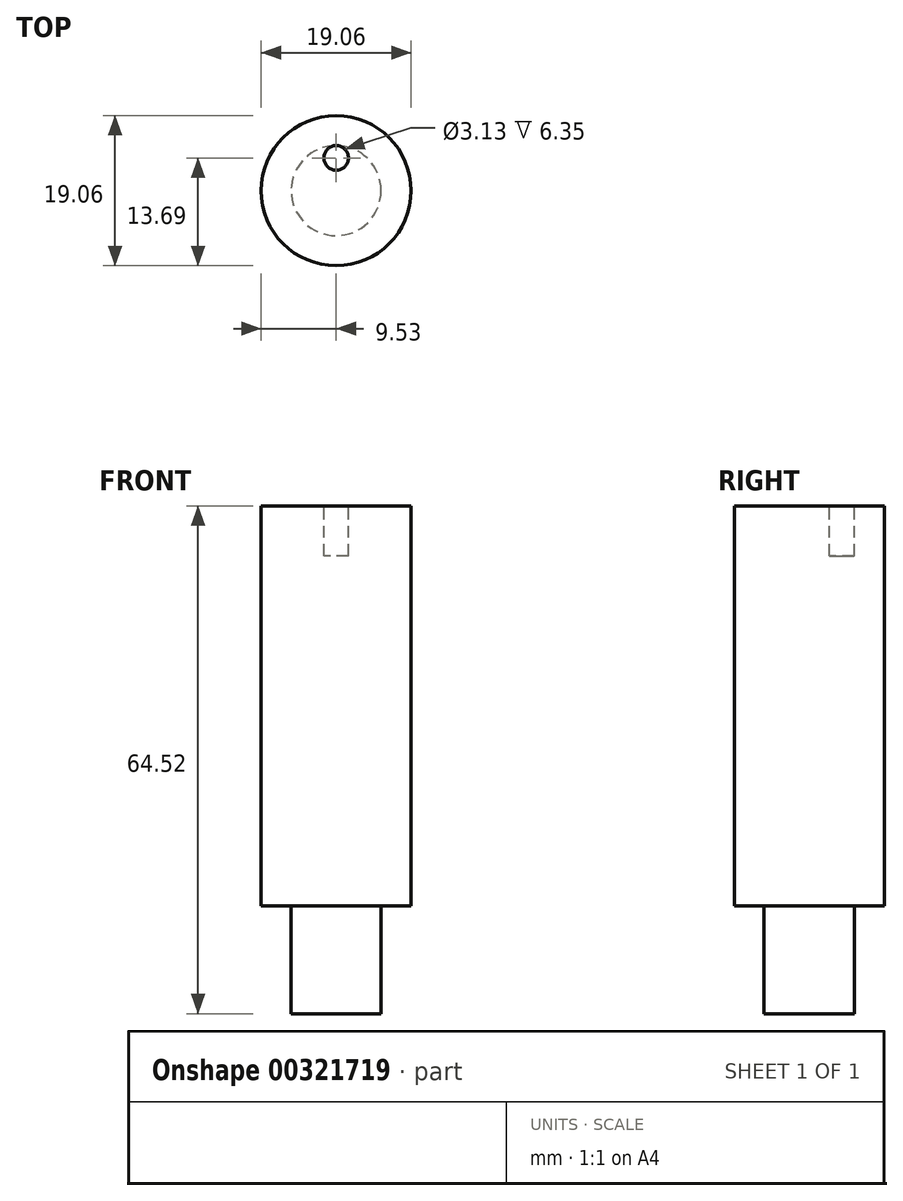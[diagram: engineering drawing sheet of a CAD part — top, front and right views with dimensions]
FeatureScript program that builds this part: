
annotation { "Feature Type Name" : "Feature", "Feature Type Description" : "" }
export const myFeature = defineFeature(function(context is Context, id is Id, definition is map)
    precondition{}
    {
        {
            var Q0;
            Q0=qCreatedBy(makeId("Top.planeOp"),FACE);
            var sketch = newSketch(context, id + "F0", { "sketchPlane" : qUnion([Q0])});
            skCircle(sketch, "E0", {"center": v(0, 0) * mm, "radius": 5.71 * mm});
            skSolve(sketch);
        }
        {
            var Q0;
            Q0=makeQuery(id+"F0.imprint","IMPRINT",FACE,{"disambiguationData":[TD([[makeQuery(id+"F0.imprint","IMPRINT",EDGE,{"derivedFrom":sQuery(id+"F0.wireOp",EDGE,"E0")}),1.0]])]});
            extrude(context, id + "F1", {"entities" : qUnion([Q0]), "depth" : 13.72 * mm});
        }
        {
            var Q0;
            Q0=makeQuery(id+"F1.opExtrude","CAP_FACE",FACE,{"disambiguationData":[OSD([sQuery(id+"F0.wireOp",EDGE,"E0")])],"isStart":false});
            var sketch = newSketch(context, id + "F2", { "sketchPlane" : qUnion([Q0])});
            skCircle(sketch, "E1", {"center": v(0, 0) * mm, "radius": 9.53 * mm});
            skSolve(sketch);
        }
        {
            var Q0;
            Q0=makeQuery(id+"F2.imprint","IMPRINT",FACE,{"disambiguationData":[TD([[makeQuery(id+"F2.imprint","IMPRINT",EDGE,{"derivedFrom":sQuery(id+"F2.wireOp",EDGE,"E1")}),1.0]])]});
            var Q1;
            Q1=makeQuery(id+"F2.imprint","IMPRINT",FACE,{"disambiguationData":[TD([[makeQuery(id+"F2.imprint","IMPRINT",EDGE,{"derivedFrom":makeQuery(id+"F1.opExtrude","CAP_EDGE",EDGE,{"disambiguationData":[OSD([sQuery(id+"F0.wireOp",EDGE,"E0")])],"isStart":false})}),1.0]])]});
            extrude(context, id + "F3", {"entities" : qUnion([Q0, Q1]), "operationType" : NewBodyOperationType.ADD, "depth" : 50.8 * mm});
        }
        {
            var Q0;
            Q0=makeQuery(id+"F3.opExtrude","CAP_FACE",FACE,{"disambiguationData":[OSD([sQuery(id+"F2.wireOp",EDGE,"E1")])],"isStart":false});
            var sketch = newSketch(context, id + "F4", { "sketchPlane" : qUnion([Q0])});
            skCircle(sketch, "E2", {"center": v(0, 4.16) * mm, "radius": 1.56 * mm});
            skSolve(sketch);
        }
        {
            var Q0;
            Q0=makeQuery(id+"F4.imprint","IMPRINT",FACE,{"disambiguationData":[TD([[makeQuery(id+"F4.imprint","IMPRINT",EDGE,{"derivedFrom":sQuery(id+"F4.wireOp",EDGE,"E2")}),1.0]])]});
            extrude(context, id + "F5", {"entities" : qUnion([Q0]), "operationType" : NewBodyOperationType.REMOVE, "oppositeDirection" : true, "depth" : 6.35 * mm});
        }
    });
